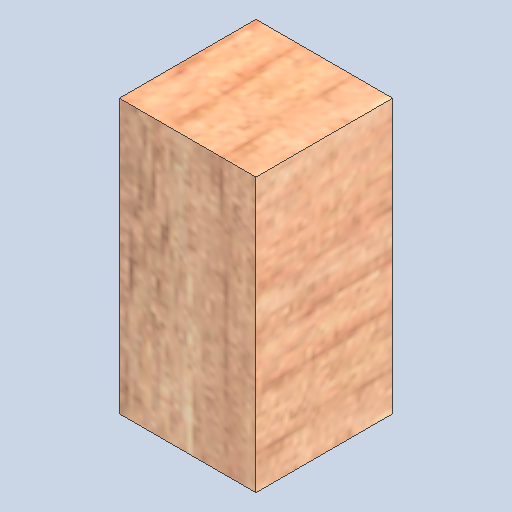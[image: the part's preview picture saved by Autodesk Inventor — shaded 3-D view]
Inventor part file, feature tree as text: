
AUTODESK INVENTOR PART (.ipt)
format: ipt  version: 2023 (Build 270158000, 158)  size: 292,352 bytes
history: native  units: mm
features: extrude x1, sketch x1
ambient origin geometry x8: Origin, YZ Plane, XZ Plane, XY Plane, X Axis, Y Axis, Z Axis, Center Point
bodies: Solid1 (feature_tree)
feature tree (2):
  extrude  "Extrusion1"  Depth=60.0mm
  sketch  "Sketch1"  dims[d0=30.0mm d1=60.0mm d2=30.0mm d3=0.0mm]
